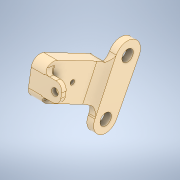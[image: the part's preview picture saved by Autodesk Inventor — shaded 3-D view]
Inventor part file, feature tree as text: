
AUTODESK INVENTOR PART (.ipt)
format: ipt  version: 2020 (Build 240168000, 168)  size: 282,624 bytes
history: native  units: in
note: dims shown in document units (in); Inventor stores cm internally (conversion verified against a paired STEP export)
features: sketch x8, extrude x5, fillet x5, projected_geometry x1
ambient origin geometry x8: Origin, YZ Plane, XZ Plane, XY Plane, X Axis, Y Axis, Z Axis, Center Point
bodies: Body1 (feature_tree)
feature tree (19):
  sketch  "Sketch3"  dims[d0=0.0039in d1=0.2362in d2=0.0in]
  sketch  "Sketch4"  dims[d3=0.315in d4=0.1575in d5=0.315in d6=0.0787in d7=0.0in d8=0.1181in]
  extrude  "Extrusion1"  Depth=0.2362in TaperAngle=0.0deg
  extrude  "Extrusion2"  Depth=0.1575in
  fillet  "Fillet1"  Radius=0.315in
  sketch  "Sketch7"  dims[d16=0.2008in d17=0.2008in]
  fillet  "Fillet2"  Radius=0.0787in
  fillet  "Fillet3"  Radius=0.1181in
  extrude  "Extrusion3"  Depth=0.1181in
  extrude  "Extrusion4"  Depth=0.0787in
  fillet  "Fillet4"  Radius=0.0787in
  fillet  "Fillet5"  Radius=0.0787in
  sketch  "Sketch9"  dims[d20=0.1969in]
  extrude  "Extrusion5"  Depth=0.2008in
  sketch  "Sketch5"  dims[d9=0.1102in d10=0.1181in]
  sketch  "Sketch6"  dims[d11=0.2047in d12=0.0787in d13=0.0787in d14=0.0787in d15=0.0in]
  sketch  "Sketch8"  dims[d18=0.1181in d19=0.0in]
  sketch  "Sketch10"  dims[d21=0.1969in d22=0.3717in d23=0.0787in d24=0.1181in d25=0.0in]
  projected_geometry  "Projected Loop2"
